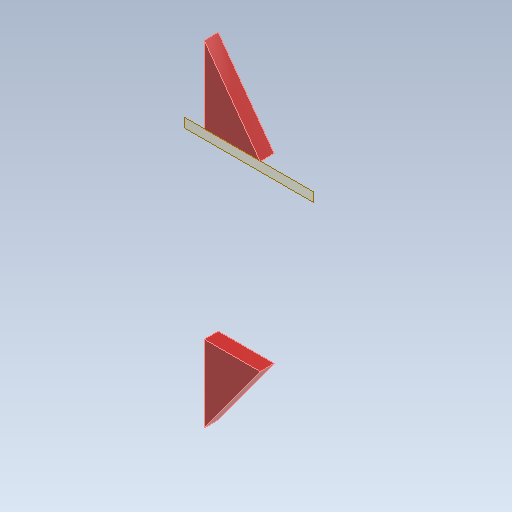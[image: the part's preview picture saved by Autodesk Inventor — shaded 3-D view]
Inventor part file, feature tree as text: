
AUTODESK INVENTOR PART (.ipt)
format: ipt  version: 2021 (Build 250183000, 183)  size: 103,424 bytes
history: native  units: in
note: dims shown in document units (in); Inventor stores cm internally (conversion verified against a paired STEP export)
features: reference x7, other x4, plane x1, extrude x1, sketch x1
ambient origin geometry x8: Origin, YZ Plane, XZ Plane, XY Plane, X Axis, Y Axis, Z Axis, Center Point
bodies: Solid1 (feature_tree)
feature tree (14):
  plane  "Work Plane1"
  extrude  "Extrusion1"  Depth=0.25in
  sketch  "Sketch1"  dims[d0=1.0in d1=1.0in d2=0.25in d3=0.0in]
  reference  "Reference1"
  reference  "Reference2"
  reference  "Reference3"
  reference  "Reference4"
  reference  "Reference5"
  reference  "Reference6"
  reference  "Reference7"
  parser-record x1  (decoder bookkeeping rows leaked as tree rows — omitted from the tree; the rows remain in map.json)
  other  "fileSocketHanger.iam"
  other  "threeStartConfigurationV01:1"
  other  "plateForFileSet:1"
note: 1 file-system path scrubbed to <path> (originals preserved in map.json)
